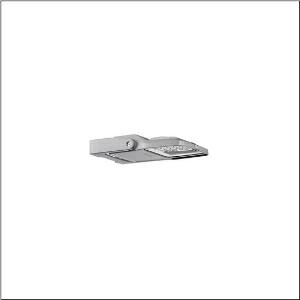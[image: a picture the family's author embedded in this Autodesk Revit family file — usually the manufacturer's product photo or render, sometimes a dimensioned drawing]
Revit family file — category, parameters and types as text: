
# Revit family: floodlight_fl_21_iq_micro___pl33t_5xa7761a2f2a_98c0
name_source: partatom
category: Lighting Fixtures
units: mm (PartAtom-declared; Revit-internal decimal feet)

## family parameters
Cut with Voids When Loaded = No
Host = Face
Light Source = No
Part Type = Normal
Room Calculation Point = No
Round Connector Dimension = Use Diameter
Shared = No

## types (1)
- --- (1 x LED, 2930 lm, 23.1 W, 3000K)
    Apparent Load = 23 VA
    CIE Flux Codes = 26 75 99 100 100
    Color Rendering = 70
    Color Temperature = 3000K
    Default Elevation = 1800 mm
    Description = Floodlight FL 21 iQ micro, floodlight, primary light control with lens, of PMMA, primary optical cover: protective disc, of toughened safety glass, transparent, light distribution: PL33T, light emission: direct distribution, installation type: surface-mounted, LED, High Power LED, rated luminous flux: 2.930lm, luminous efficacy: 127lm/W, light colour: 730, colour temperature: 3000K, control: optimised constant luminous flux control (CLO 2.0), Desk-Remote (wireless, voltage-free reading and setting of iQ features in the workshop via application-optimized NFC function/RFID function), Light-Fading, Smart-Wire, Night-Set, Lumen-Switch, Temp-Guard, Auto-Match, with terminal, 6-pole, mains connection: 220..240V, AC, 50/60Hz, start of lifetime: 23W, end of service life: 24W, reduction: 11W, luminaire housing, of diecast aluminium, powder-coated, Siteco® metallic grey (DB 702S), corrosivity category C5 mid according to DIN EN ISO 12944, sealing non-destructively replaceable, design bracket, of diecast aluminium, powder-coated, Siteco® metallic grey (DB 702S), protection rating (complete): IP66, insulation class (complete): insulation class II (safety insulation), certification: CE, ENEC, VDE, protection symbol: D, impact resistance: IK07, permissible operating ambient temperature: -40..+40°C, permissible operating ambient temperature for outdoor applications: -40..+50°C, standard: DIN EN 12944, LABS conformity tested according to VDMA 24364:2018-05, packaging unit: 1 piece

Light Distribution: PL33T
    Height = 65 mm
    Lamp = 1 x LED
    Lamp Light Flux = 2930 lm
    Lamp Power = 23.1 W
    Lamp count = 1
    Length = 312 mm
    Luminous efficacy = 127 lm/W
    Manufacturer = Siteco
    ModVariant = No
    Model = 5XA7761A2F2A
    Mounting Place = Wall
    Mounting Type = Surface mounted
    Number of Poles = 1
    OnlyDefault = Yes
    Power Factor = 1
    Product Name = Floodlight FL 21 iQ micro | PL33T
    Product group = floodlight | wall mounted
    ProductGroupID = 2001
    Protection Class = Protection class II
    Protection Degree = IP 66
    RLX_Detail_Level = 1
    RLX_Emergency_Light_Flux = 0 lm
    RLX_Emergency_Type = 0
    RLX_Emergency_Type_DB = No
    RlxData = <blob elided: 97325 chars, md5=366665d8>
    Socket = socket
    Standby Power = 0 W
    System Light Flux = 2930 lm
    System Power = 23 W
    Type Comments = factory setting: luminous flux: 100 % | dim-lin: 254 | 455 mA
    Type Image = l_1006878.jpg
    URL = http://relux.com
    VarID = @adj_080745
    Voltage = 0 V
    Weight = 0.00 kg
    Width = 230 mm

## geometry (parser evidence)
native form markers: Blend x4, Sweep x12
no freeform markers — native parametric forms only
